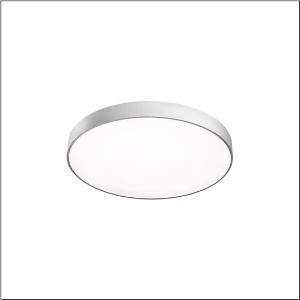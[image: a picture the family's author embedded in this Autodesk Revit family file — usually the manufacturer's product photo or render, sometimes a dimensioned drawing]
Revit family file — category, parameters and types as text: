
# Revit family: round_21_m_51mr36fd0321s
name_source: partatom
category: Lighting Fixtures
units: mm (PartAtom-declared; Revit-internal decimal feet)

## family parameters
Cut with Voids When Loaded = No
Host = Face
Light Source = No
Part Type = Normal
Room Calculation Point = No
Round Connector Dimension = Use Diameter
Shared = No

## types (1)
- Round 21 M (1 x LED, 7500 lm, 54.9 W, 3000K)
    Apparent Load = 55 VA
    CIE Flux Codes = 49 80 96 100 100
    Color Rendering = 80
    Color Temperature = 3000K
    Default Elevation = 1800 mm
    Description = Round 21 M, wall and ceiling luminaire, primary optical cover: cover, of PMMA, opal, light emission: direct distribution, primary light characteristic: symmetric, installation type: suspended mounting, surface-mounted, LED, rated luminous flux: 6.790lm, luminous efficacy: 124lm/W, light colour: 830, colour temperature: 3000K, with terminal, 5-pole, mains connection: 230V, AC, 50/60Hz, rated input power: 55W, housing, of aluminium, coated, silver, diameter: 600mm, height: 62mm, protection rating (complete): IP40, insulation class (complete): insulation class I (protective earthing), certification: CE, impact resistance: IK04, permissible operating ambient temperature: -10..+35°C, packaging unit: 1 piece
    Height = 87 mm
    Lamp = 1 x LED
    Lamp Light Flux = 7500 lm
    Lamp Power = 54.9 W
    Lamp count = 1
    Length = 600 mm
    Luminous efficacy = 137 lm/W
    Manufacturer = Siteco
    ModVariant = No
    Model = 51MR36FD0321S
    Mounting Place = Ceiling
    Mounting Type = Surface mounted
    Number of Poles = 1
    OnlyDefault = Yes
    Power Factor = 1
    Product Name = Round 21 M
    Product group = wall and ceiling luminaire
    ProductGroupID = 303
    Protection Class = Protection class I
    Protection Degree = IP 40
    RLX_Detail_Level = 1
    RLX_Emergency_Light_Flux = 0 lm
    RLX_Emergency_Type = 0
    RLX_Emergency_Type_DB = No
    RlxData = <blob elided: 14789 chars, md5=d00e99c3>
    Socket = socket
    Standby Power = 0 W
    System Light Flux = 7500 lm
    System Power = 55 W
    Type Comments = Product without accessories
    Type Image = l_1258303.jpg
    URL = http://relux.com
    VarID = ---
    Voltage = 0 V
    Weight = 0.00 kg
    Width = 0 mm  [stored 0 ft]

note: [stored X ft] marks values corroborated as IEEE doubles in the binary element streams (Revit-internal decimal feet)

## geometry (parser evidence)
native form markers: Sweep x11
no freeform markers — native parametric forms only
